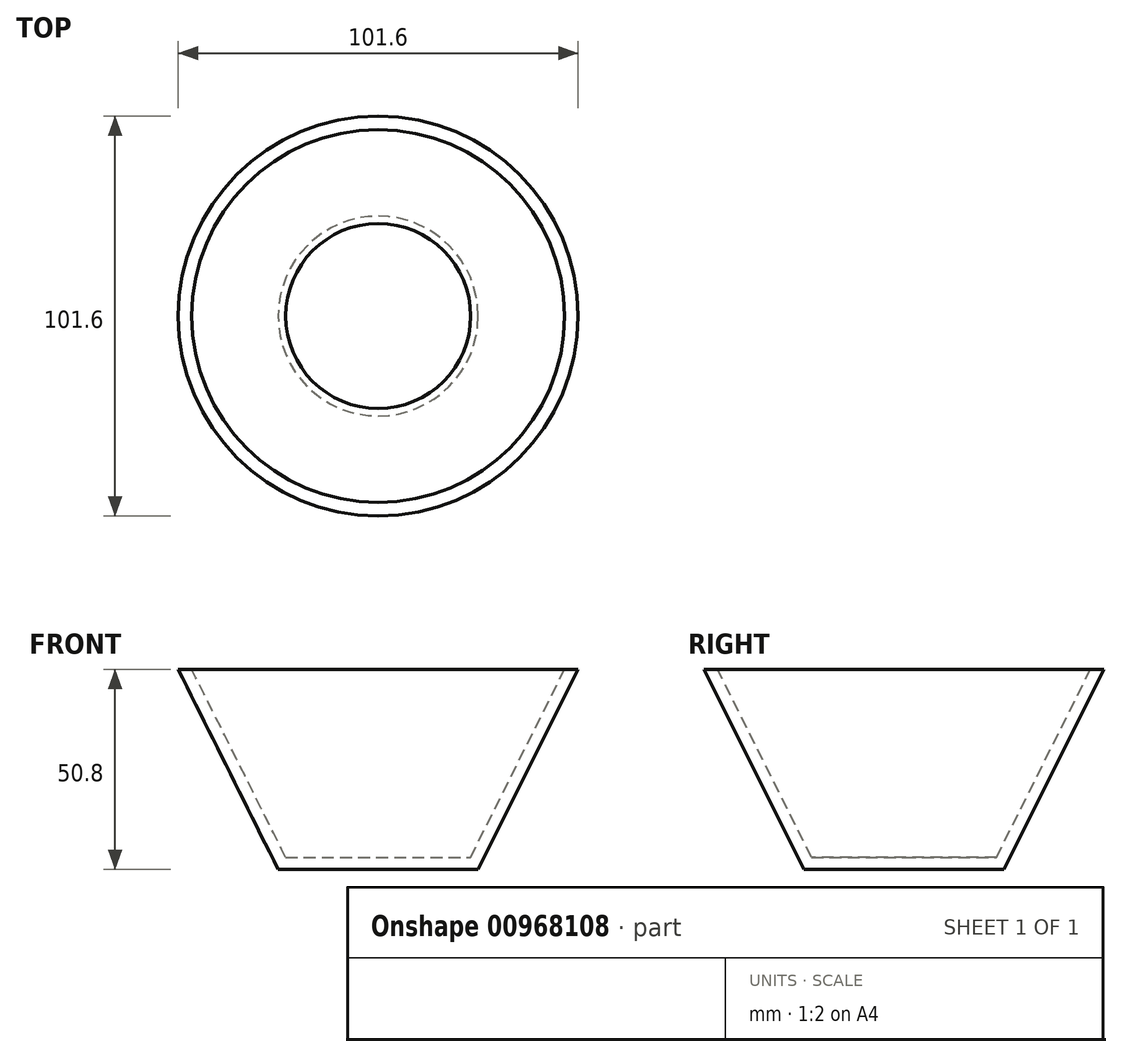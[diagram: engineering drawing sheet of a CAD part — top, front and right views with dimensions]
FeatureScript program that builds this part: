
annotation { "Feature Type Name" : "Feature", "Feature Type Description" : "" }
export const myFeature = defineFeature(function(context is Context, id is Id, definition is map)
    precondition{}
    {
        {
            var Q0;
            Q0=qCreatedBy(makeId("Front.planeOp"),FACE);
            var sketch = newSketch(context, id + "F0", { "sketchPlane" : qUnion([Q0])});
            skLineSegment(sketch, "E0", {"start": v(0, 0) * mm, "end": v(0, 50.8) * mm, "construction": true});
            skLineSegment(sketch, "E1", {"start": v(0, 0) * mm, "end": v(25.4, 0) * mm});
            skLineSegment(sketch, "E2", {"start": v(25.4, 0) * mm, "end": v(50.8, 50.8) * mm});
            skLineSegment(sketch, "E3.0", {"start": v(23.5, 3.07) * mm, "end": v(47.36, 50.8) * mm});
            skLineSegment(sketch, "E3.1", {"start": v(0, 3.07) * mm, "end": v(23.5, 3.07) * mm});
            skLineSegment(sketch, "E4", {"start": v(0, 3.07) * mm, "end": v(0, 0) * mm});
            skLineSegment(sketch, "E5", {"start": v(47.36, 50.8) * mm, "end": v(50.8, 50.8) * mm});
            skSolve(sketch);
        }
        {
            var Q0;
            Q0=makeQuery(id+"F0.imprint","IMPRINT",FACE,{"disambiguationData":[TD([[makeQuery(id+"F0.imprint","IMPRINT",EDGE,{"derivedFrom":sQuery(id+"F0.wireOp",EDGE,"E1")}),1.0]])]});
            var Q1;
            Q1=sQuery(id+"F0.wireOp",EDGE,"E0");
            revolve(context, id + "F1", {"surfaceOperationType" : NewSurfaceOperationType.NEW, "entities" : qUnion([Q0]), "axis" : qUnion([Q1]), "revolveType" : RevolveType.FULL});
        }
    });
